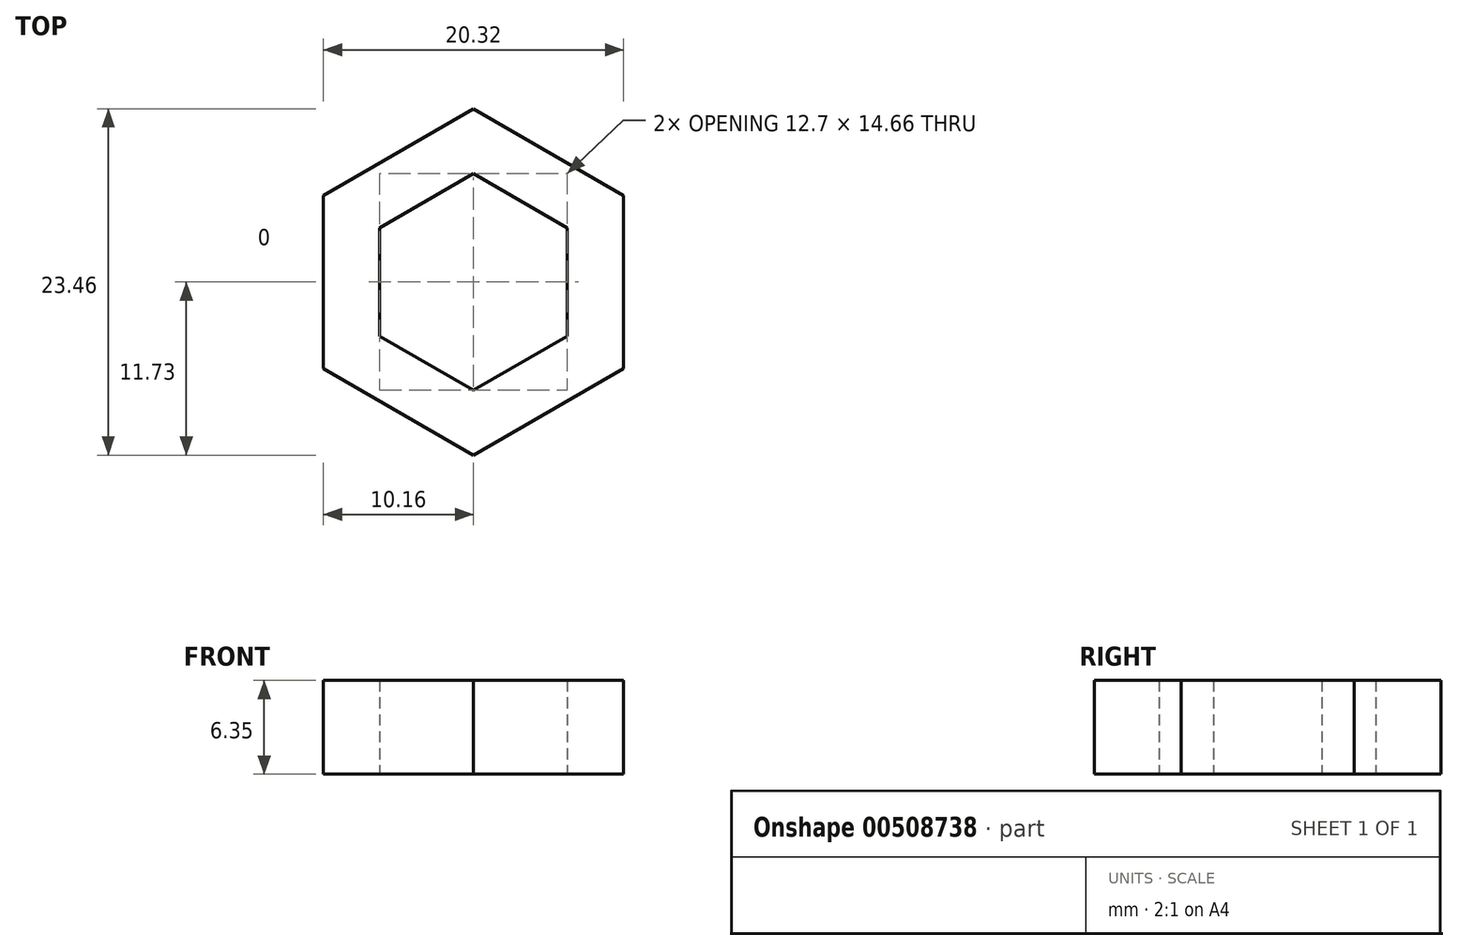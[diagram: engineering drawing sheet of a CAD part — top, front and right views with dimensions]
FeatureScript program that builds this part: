
annotation { "Feature Type Name" : "Feature", "Feature Type Description" : "" }
export const myFeature = defineFeature(function(context is Context, id is Id, definition is map)
    precondition{}
    {
        {
            var Q0;
            Q0=qCreatedBy(makeId("Top.planeOp"),FACE);
            var sketch = newSketch(context, id + "F0", { "sketchPlane" : qUnion([Q0])});
            skCircle(sketch, "E0.cCircle", {"center": v(0, 0) * mm, "radius": 6.35 * mm, "construction": true});
            skLineSegment(sketch, "E0.0", {"start": v(6.35, 3.67) * mm, "end": v(6.35, -3.67) * mm});
            skLineSegment(sketch, "E0.1", {"start": v(6.35, -3.67) * mm, "end": v(0, -7.33) * mm});
            skLineSegment(sketch, "E0.2", {"start": v(0, -7.33) * mm, "end": v(-6.35, -3.67) * mm});
            skLineSegment(sketch, "E0.3", {"start": v(-6.35, -3.67) * mm, "end": v(-6.35, 3.67) * mm});
            skLineSegment(sketch, "E0.4", {"start": v(-6.35, 3.67) * mm, "end": v(0, 7.33) * mm});
            skLineSegment(sketch, "E0.5", {"start": v(0, 7.33) * mm, "end": v(6.35, 3.67) * mm});
            skPoint(sketch, "E0.0.midPoint", {"position": v(6.35, 0) * mm});
            skLineSegment(sketch, "E1.0", {"start": v(-10.16, 5.87) * mm, "end": v(0, 11.73) * mm});
            skLineSegment(sketch, "E1.1", {"start": v(10.16, 5.87) * mm, "end": v(10.16, -5.87) * mm});
            skLineSegment(sketch, "E1.2", {"start": v(10.16, -5.87) * mm, "end": v(0, -11.73) * mm});
            skLineSegment(sketch, "E1.3", {"start": v(0, 11.73) * mm, "end": v(10.16, 5.87) * mm});
            skLineSegment(sketch, "E1.4", {"start": v(0, -11.73) * mm, "end": v(-10.16, -5.87) * mm});
            skLineSegment(sketch, "E1.5", {"start": v(-10.16, -5.87) * mm, "end": v(-10.16, 5.87) * mm});
            skSolve(sketch);
        }
        {
            var Q0;
            Q0=makeQuery(id+"F0.imprint","IMPRINT",FACE,{"disambiguationData":[TD([[makeQuery(id+"F0.imprint","IMPRINT",EDGE,{"derivedFrom":sQuery(id+"F0.wireOp",EDGE,"E0.0")}),1.0]])]});
            extrude(context, id + "F1", {"entities" : qUnion([Q0]), "depth" : 6.35 * mm});
        }
    });
